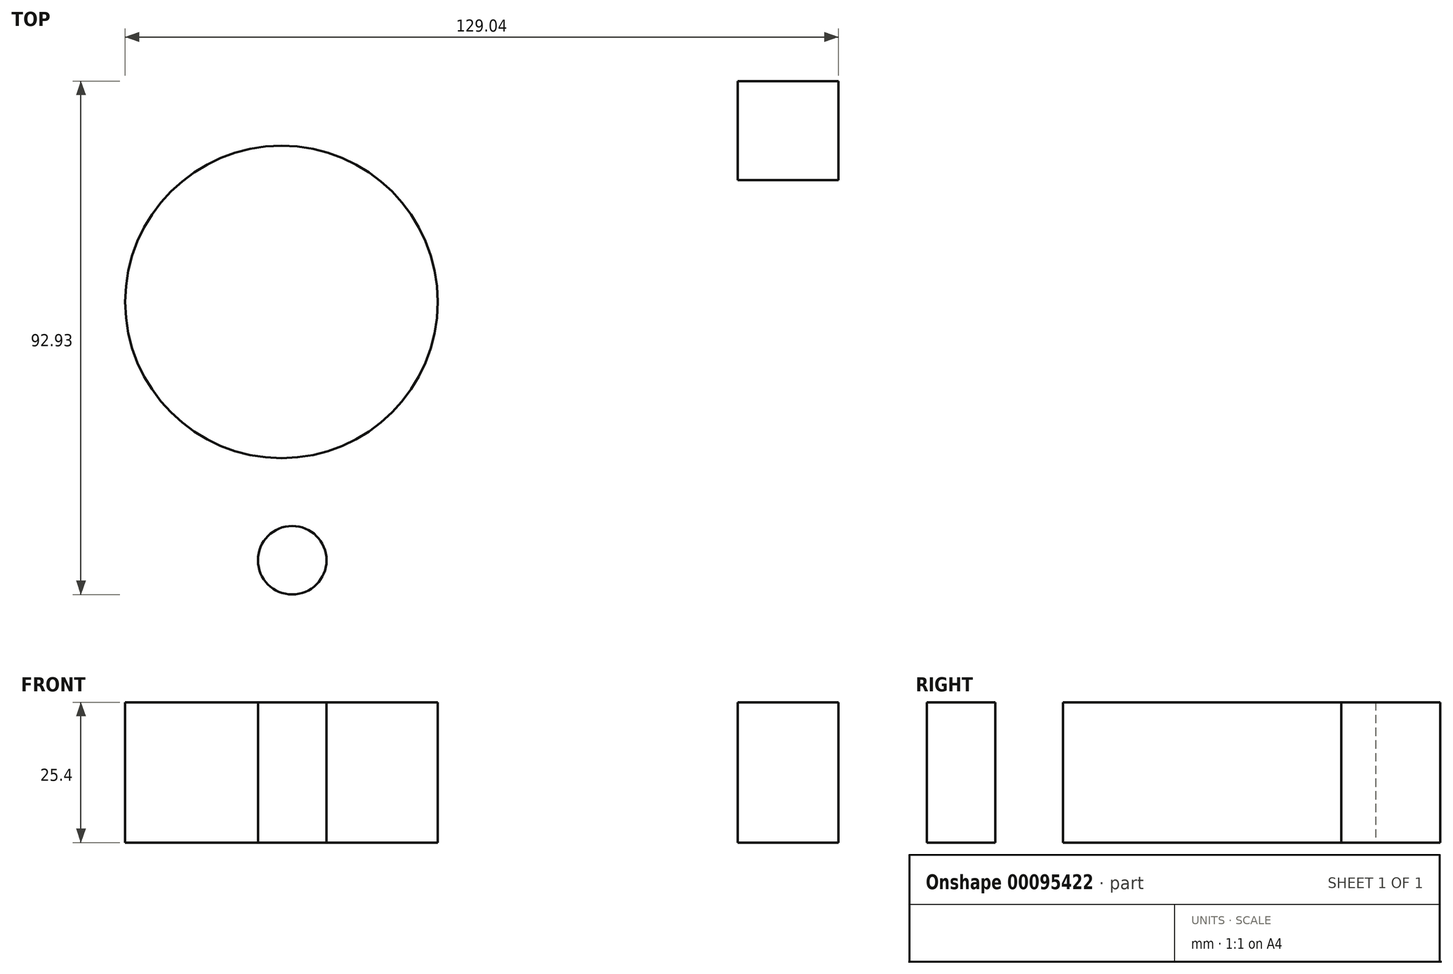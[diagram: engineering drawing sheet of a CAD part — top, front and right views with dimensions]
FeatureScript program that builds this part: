
annotation { "Feature Type Name" : "Feature", "Feature Type Description" : "" }
export const myFeature = defineFeature(function(context is Context, id is Id, definition is map)
    precondition{}
    {
        {
            var Q0;
            Q0=qCreatedBy(makeId("Top.planeOp"),FACE);
            var sketch = newSketch(context, id + "F0", { "sketchPlane" : qUnion([Q0])});
            skCircle(sketch, "E0", {"center": v(-87.91, 12.63) * mm, "radius": 6.2 * mm});
            skCircle(sketch, "E1", {"center": v(-89.85, 59.4) * mm, "radius": 28.28 * mm});
            skLineSegment(sketch, "E2.bottom", {"start": v(10.9, 99.35) * mm, "end": v(-7.26, 99.35) * mm});
            skLineSegment(sketch, "E2.top", {"start": v(10.9, 81.43) * mm, "end": v(-7.26, 81.43) * mm});
            skLineSegment(sketch, "E2.left", {"start": v(10.9, 99.35) * mm, "end": v(10.9, 81.43) * mm});
            skLineSegment(sketch, "E2.right", {"start": v(-7.26, 99.35) * mm, "end": v(-7.26, 81.43) * mm});
            skPoint(sketch, "E2.middle", {"position": v(1.82, 90.39) * mm});
            skSolve(sketch);
        }
        {
            var Q0;
            Q0 = qSketchRegion(id + "F0", true);
            extrude(context, id + "F1", {"entities" : qUnion([Q0]), "depth" : 25.4 * mm});
        }
    });
